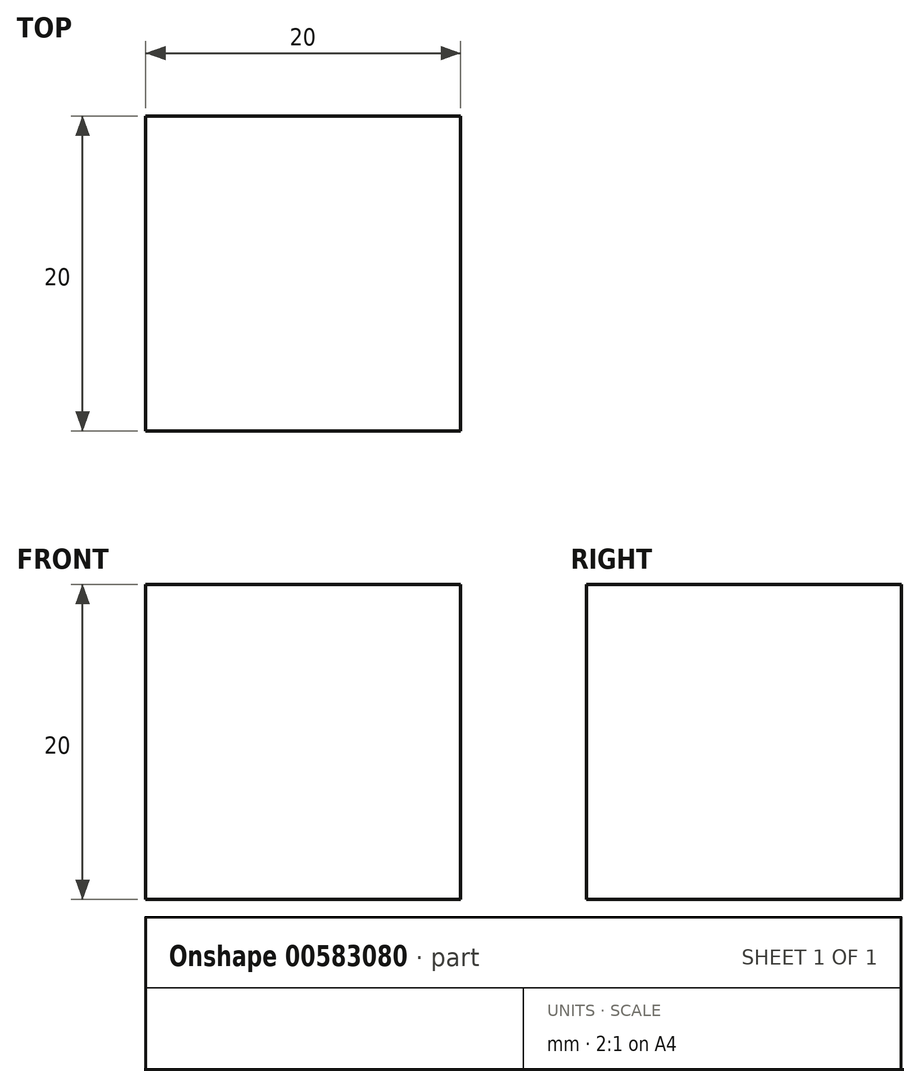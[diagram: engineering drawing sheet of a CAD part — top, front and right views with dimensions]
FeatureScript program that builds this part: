
annotation { "Feature Type Name" : "Feature", "Feature Type Description" : "" }
export const myFeature = defineFeature(function(context is Context, id is Id, definition is map)
    precondition{}
    {
        {
            var Q0;
            Q0=qCreatedBy(makeId("Top.planeOp"),FACE);
            var sketch = newSketch(context, id + "F0", { "sketchPlane" : qUnion([Q0])});
            skLineSegment(sketch, "E0.bottom", {"start": v(-10, 10) * mm, "end": v(10, 10) * mm});
            skLineSegment(sketch, "E0.top", {"start": v(-10, -10) * mm, "end": v(10, -10) * mm});
            skLineSegment(sketch, "E0.left", {"start": v(-10, 10) * mm, "end": v(-10, -10) * mm});
            skLineSegment(sketch, "E0.right", {"start": v(10, 10) * mm, "end": v(10, -10) * mm});
            skLineSegment(sketch, "E1.bottom", {"start": v(0, 10) * mm, "end": v(0, 10) * mm});
            skLineSegment(sketch, "E1.top", {"start": v(0, -10) * mm, "end": v(0, -10) * mm});
            skLineSegment(sketch, "E1.left", {"start": v(0, 10) * mm, "end": v(0, -10) * mm, "construction": true});
            skLineSegment(sketch, "E1.right", {"start": v(0, 10) * mm, "end": v(0, -10) * mm, "construction": true});
            skLineSegment(sketch, "E2.bottom", {"start": v(-10, 0) * mm, "end": v(10, 0) * mm, "construction": true});
            skLineSegment(sketch, "E2.top", {"start": v(-10, 0) * mm, "end": v(10, 0) * mm, "construction": true});
            skLineSegment(sketch, "E2.left", {"start": v(-10, 0) * mm, "end": v(-10, 0) * mm});
            skLineSegment(sketch, "E2.right", {"start": v(10, 0) * mm, "end": v(10, 0) * mm});
            skSolve(sketch);
        }
        {
            var Q0;
            Q0 = qSketchRegion(id + "F0", true);
            extrude(context, id + "F1", {"entities" : qUnion([Q0]), "depth" : 20 * mm, "offsetDistance" : 25 * mm});
        }
    });
